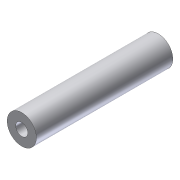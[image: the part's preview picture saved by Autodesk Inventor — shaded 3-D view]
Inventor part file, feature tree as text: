
AUTODESK INVENTOR PART (.ipt)
format: ipt  version: 2012 (Build 160160000, 160)  size: 79,360 bytes
history: native  units: in
note: dims shown in document units (in); Inventor stores cm internally (conversion verified against a paired STEP export)
features: extrude x1, sketch x1
ambient origin geometry x8: Origin, YZ Plane, XZ Plane, XY Plane, X Axis, Y Axis, Z Axis, Center Point
bodies: Solid1 (feature_tree)
feature tree (2):
  extrude  "Extrusion1"  Depth=0.625in
  sketch  "Sketch1"  dims[d0=1.5in d1=0.625in d2=7.0in d3=0.0in]
